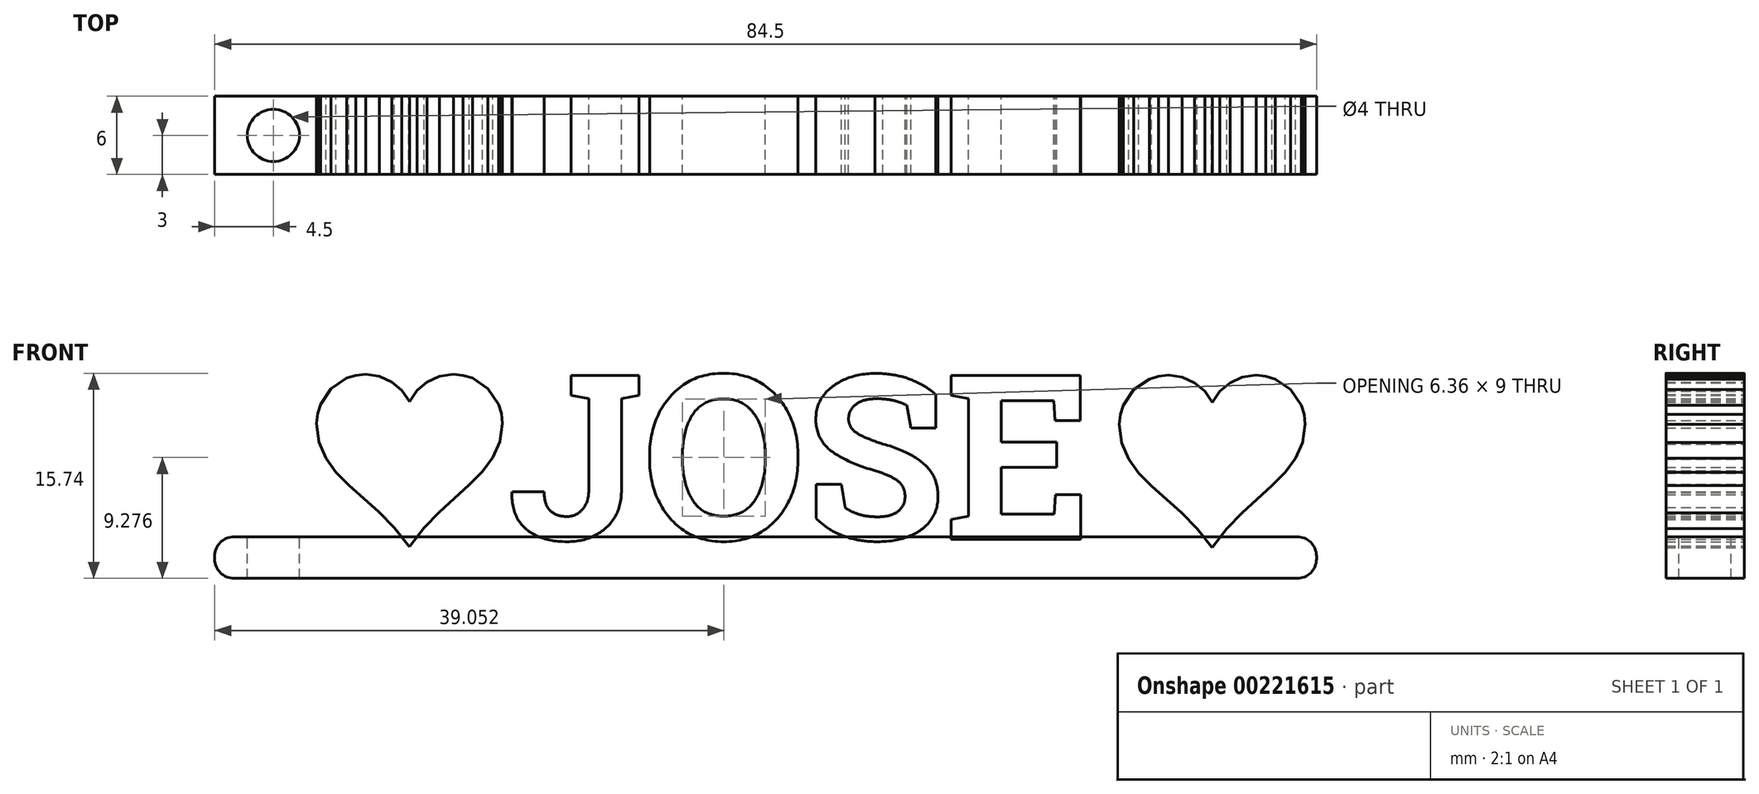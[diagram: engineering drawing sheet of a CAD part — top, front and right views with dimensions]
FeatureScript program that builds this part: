
annotation { "Feature Type Name" : "Feature", "Feature Type Description" : "" }
export const myFeature = defineFeature(function(context is Context, id is Id, definition is map)
    precondition{}
    {
        {
            var Q0;
            Q0=qCreatedBy(makeId("Front.planeOp"),FACE);
            var sketch = newSketch(context, id + "F0", { "sketchPlane" : qUnion([Q0])});
            skText(sketch, "E0", { "text": "   JOSE", "fontName": "RobotoSlab-Bold.ttf"});
            skLineSegment(sketch, "E1", {"start": v(45.25, 12.6) * mm, "end": v(44.49, 12.52) * mm});
            skLineSegment(sketch, "E2", {"start": v(44.49, 12.52) * mm, "end": v(43.78, 12.3) * mm});
            skLineSegment(sketch, "E3", {"start": v(43.78, 12.3) * mm, "end": v(42.58, 11.5) * mm});
            skLineSegment(sketch, "E4", {"start": v(42.58, 11.5) * mm, "end": v(41.78, 10.3) * mm});
            skLineSegment(sketch, "E5", {"start": v(41.78, 10.3) * mm, "end": v(41.56, 9.59) * mm});
            skLineSegment(sketch, "E6", {"start": v(41.56, 9.59) * mm, "end": v(41.48, 8.83) * mm});
            skLineSegment(sketch, "E7", {"start": v(41.48, 8.83) * mm, "end": v(41.67, 7.39) * mm});
            skLineSegment(sketch, "E8", {"start": v(41.67, 7.39) * mm, "end": v(42.19, 6.16) * mm});
            skLineSegment(sketch, "E9", {"start": v(42.19, 6.16) * mm, "end": v(42.98, 5.08) * mm});
            skLineSegment(sketch, "E10", {"start": v(42.98, 5.08) * mm, "end": v(43.96, 4.08) * mm});
            skLineSegment(sketch, "E11", {"start": v(43.96, 4.08) * mm, "end": v(46.26, 2.03) * mm});
            skLineSegment(sketch, "E12", {"start": v(46.26, 2.03) * mm, "end": v(47.44, 0.82) * mm});
            skLineSegment(sketch, "E13", {"start": v(47.44, 0.82) * mm, "end": v(48.56, -0.59) * mm});
            skLineSegment(sketch, "E14", {"start": v(48.56, -0.59) * mm, "end": v(48.6, -0.65) * mm});
            skLineSegment(sketch, "E15", {"start": v(48.6, -0.65) * mm, "end": v(48.65, -0.59) * mm});
            skLineSegment(sketch, "E16", {"start": v(48.65, -0.59) * mm, "end": v(49.73, 0.82) * mm});
            skLineSegment(sketch, "E17", {"start": v(49.73, 0.82) * mm, "end": v(50.9, 2.03) * mm});
            skLineSegment(sketch, "E18", {"start": v(50.9, 2.03) * mm, "end": v(53.2, 4.12) * mm});
            skLineSegment(sketch, "E19", {"start": v(53.2, 4.12) * mm, "end": v(54.2, 5.13) * mm});
            skLineSegment(sketch, "E20", {"start": v(54.2, 5.13) * mm, "end": v(55, 6.21) * mm});
            skLineSegment(sketch, "E21", {"start": v(55, 6.21) * mm, "end": v(55.54, 7.42) * mm});
            skLineSegment(sketch, "E22", {"start": v(55.54, 7.42) * mm, "end": v(55.73, 8.83) * mm});
            skLineSegment(sketch, "E23", {"start": v(55.73, 8.83) * mm, "end": v(55.66, 9.59) * mm});
            skLineSegment(sketch, "E24", {"start": v(55.66, 9.59) * mm, "end": v(55.44, 10.3) * mm});
            skLineSegment(sketch, "E25", {"start": v(55.44, 10.3) * mm, "end": v(54.63, 11.5) * mm});
            skLineSegment(sketch, "E26", {"start": v(54.63, 11.5) * mm, "end": v(53.43, 12.3) * mm});
            skLineSegment(sketch, "E27", {"start": v(53.43, 12.3) * mm, "end": v(52.72, 12.52) * mm});
            skLineSegment(sketch, "E28", {"start": v(52.72, 12.52) * mm, "end": v(51.97, 12.6) * mm});
            skLineSegment(sketch, "E29", {"start": v(51.97, 12.6) * mm, "end": v(50.9, 12.44) * mm});
            skLineSegment(sketch, "E30", {"start": v(50.9, 12.44) * mm, "end": v(49.96, 12.01) * mm});
            skLineSegment(sketch, "E31", {"start": v(49.96, 12.01) * mm, "end": v(49.18, 11.35) * mm});
            skLineSegment(sketch, "E32", {"start": v(49.18, 11.35) * mm, "end": v(48.6, 10.5) * mm});
            skLineSegment(sketch, "E33", {"start": v(48.6, 10.5) * mm, "end": v(48.03, 11.35) * mm});
            skLineSegment(sketch, "E34", {"start": v(48.03, 11.35) * mm, "end": v(47.25, 12.01) * mm});
            skLineSegment(sketch, "E35", {"start": v(47.25, 12.01) * mm, "end": v(46.3, 12.44) * mm});
            skLineSegment(sketch, "E36", {"start": v(46.3, 12.44) * mm, "end": v(45.25, 12.6) * mm});
            skLineSegment(sketch, "E37", {"start": v(39.6, 12.72) * mm, "end": v(70.68, 12.72) * mm, "construction": true});
            skLineSegment(sketch, "E38", {"start": v(-16.32, 12.66) * mm, "end": v(-17.08, 12.59) * mm});
            skLineSegment(sketch, "E39", {"start": v(-17.08, 12.59) * mm, "end": v(-17.78, 12.37) * mm});
            skLineSegment(sketch, "E40", {"start": v(-17.78, 12.37) * mm, "end": v(-18.98, 11.56) * mm});
            skLineSegment(sketch, "E41", {"start": v(-18.98, 11.56) * mm, "end": v(-19.79, 10.36) * mm});
            skLineSegment(sketch, "E42", {"start": v(-19.79, 10.36) * mm, "end": v(-20, 9.65) * mm});
            skLineSegment(sketch, "E43", {"start": v(-20, 9.65) * mm, "end": v(-20.09, 8.9) * mm});
            skLineSegment(sketch, "E44", {"start": v(-20.09, 8.9) * mm, "end": v(-19.9, 7.45) * mm});
            skLineSegment(sketch, "E45", {"start": v(-19.9, 7.45) * mm, "end": v(-19.38, 6.22) * mm});
            skLineSegment(sketch, "E46", {"start": v(-19.38, 6.22) * mm, "end": v(-18.6, 5.15) * mm});
            skLineSegment(sketch, "E47", {"start": v(-18.6, 5.15) * mm, "end": v(-17.6, 4.15) * mm});
            skLineSegment(sketch, "E48", {"start": v(-17.6, 4.15) * mm, "end": v(-15.31, 2.09) * mm});
            skLineSegment(sketch, "E49", {"start": v(-15.31, 2.09) * mm, "end": v(-14.13, 0.89) * mm});
            skLineSegment(sketch, "E50", {"start": v(-14.13, 0.89) * mm, "end": v(-13, -0.52) * mm});
            skLineSegment(sketch, "E51", {"start": v(-13, -0.52) * mm, "end": v(-12.96, -0.59) * mm});
            skLineSegment(sketch, "E52", {"start": v(-12.96, -0.59) * mm, "end": v(-12.92, -0.52) * mm});
            skLineSegment(sketch, "E53", {"start": v(-12.92, -0.52) * mm, "end": v(-11.84, 0.89) * mm});
            skLineSegment(sketch, "E54", {"start": v(-11.84, 0.89) * mm, "end": v(-10.67, 2.1) * mm});
            skLineSegment(sketch, "E55", {"start": v(-10.67, 2.1) * mm, "end": v(-8.37, 4.19) * mm});
            skLineSegment(sketch, "E56", {"start": v(-8.37, 4.19) * mm, "end": v(-7.37, 5.2) * mm});
            skLineSegment(sketch, "E57", {"start": v(-7.37, 5.2) * mm, "end": v(-6.56, 6.28) * mm});
            skLineSegment(sketch, "E58", {"start": v(-6.56, 6.28) * mm, "end": v(-6.03, 7.49) * mm});
            skLineSegment(sketch, "E59", {"start": v(-6.03, 7.49) * mm, "end": v(-5.83, 8.9) * mm});
            skLineSegment(sketch, "E60", {"start": v(-5.83, 8.9) * mm, "end": v(-5.91, 9.65) * mm});
            skLineSegment(sketch, "E61", {"start": v(-5.91, 9.65) * mm, "end": v(-6.13, 10.36) * mm});
            skLineSegment(sketch, "E62", {"start": v(-6.13, 10.36) * mm, "end": v(-6.94, 11.56) * mm});
            skLineSegment(sketch, "E63", {"start": v(-6.94, 11.56) * mm, "end": v(-8.13, 12.37) * mm});
            skLineSegment(sketch, "E64", {"start": v(-8.13, 12.37) * mm, "end": v(-8.84, 12.59) * mm});
            skLineSegment(sketch, "E65", {"start": v(-8.84, 12.59) * mm, "end": v(-9.6, 12.66) * mm});
            skLineSegment(sketch, "E66", {"start": v(-9.6, 12.66) * mm, "end": v(-10.66, 12.5) * mm});
            skLineSegment(sketch, "E67", {"start": v(-10.66, 12.5) * mm, "end": v(-11.6, 12.08) * mm});
            skLineSegment(sketch, "E68", {"start": v(-11.6, 12.08) * mm, "end": v(-12.38, 11.41) * mm});
            skLineSegment(sketch, "E69", {"start": v(-12.38, 11.41) * mm, "end": v(-12.96, 10.56) * mm});
            skLineSegment(sketch, "E70", {"start": v(-12.96, 10.56) * mm, "end": v(-13.54, 11.41) * mm});
            skLineSegment(sketch, "E71", {"start": v(-13.54, 11.41) * mm, "end": v(-14.32, 12.08) * mm});
            skLineSegment(sketch, "E72", {"start": v(-14.32, 12.08) * mm, "end": v(-15.26, 12.5) * mm});
            skLineSegment(sketch, "E73", {"start": v(-15.26, 12.5) * mm, "end": v(-16.32, 12.66) * mm});
            const initialGuessF0  = {"E0": [-0.0184, 0, 1, 0, 0.01272]};
            skSetInitialGuess(sketch, initialGuessF0);
            skSolve(sketch);
        }
        {
            var Q0;
            Q0=qSketchRegion(id+"F0",true);
            extrude(context, id + "F1", {"entities" : qUnion([Q0]), "endBound" : BoundingType.SYMMETRIC, "depth" : 6 * mm});
        }
        {
            var Q0;
            Q0=qCreatedBy(makeId("Top.planeOp"),FACE);
            var sketch = newSketch(context, id + "F2", { "sketchPlane" : qUnion([Q0])});
            skLineSegment(sketch, "E74.bottom", {"start": v(-20.4, 3) * mm, "end": v(56.6, 3) * mm});
            skLineSegment(sketch, "E74.top", {"start": v(-20.4, -3) * mm, "end": v(56.6, -3) * mm});
            skLineSegment(sketch, "E74.left", {"start": v(-20.4, 3) * mm, "end": v(-20.4, -3) * mm});
            skLineSegment(sketch, "E74.right", {"start": v(56.6, 3) * mm, "end": v(56.6, -3) * mm});
            skSolve(sketch);
        }
        {
            var Q0;
            Q0=makeQuery(id+"F2.imprint","IMPRINT",FACE,{"disambiguationData":[TD([[makeQuery(id+"F2.imprint","IMPRINT",EDGE,{"derivedFrom":sQuery(id+"F2.wireOp",EDGE,"E74.bottom")}),-1.0]])]});
            extrude(context, id + "F3", {"entities" : qUnion([Q0]), "depth" : 0.2 * mm});
        }
        {
            var Q0;
            Q0=makeQuery(id+"F3.opExtrude","CAP_FACE",FACE,{"disambiguationData":[OSD([sQuery(id+"F2.wireOp",EDGE,"E74.bottom"),sQuery(id+"F2.wireOp",EDGE,"E74.top"),sQuery(id+"F2.wireOp",EDGE,"E74.left"),sQuery(id+"F2.wireOp",EDGE,"E74.right")])],"isStart":true});
            extrude(context, id + "F4", {"entities" : qUnion([Q0]), "depth" : 3 * mm});
        }
        {
            var Q0;
            {var subQ0=sQuery(id+"F2.wireOp",EDGE,"E74.left");Q0=makeQuery(id+"FaVoHrOpcFZXiYX_6.opBoolean","MERGE",FACE,{"derivedFrom":[makeQuery(id+"F3.opExtrude","SWEPT_FACE",FACE,{"disambiguationData":[OSD([subQ0])]}),makeQuery(id+"F4.opExtrude","SWEPT_FACE",FACE,{"disambiguationData":[OSD([subQ0])]})]});}
            var sketch = newSketch(context, id + "F5", { "sketchPlane" : qUnion([Q0])});
            skLineSegment(sketch, "E75.bottom", {"start": v(-3, -3) * mm, "end": v(3, -3) * mm});
            skLineSegment(sketch, "E75.top", {"start": v(-3, 0.2) * mm, "end": v(3, 0.2) * mm});
            skLineSegment(sketch, "E75.left", {"start": v(-3, -3) * mm, "end": v(-3, 0.2) * mm});
            skLineSegment(sketch, "E75.right", {"start": v(3, -3) * mm, "end": v(3, 0.2) * mm});
            skSolve(sketch);
        }
        {
            var Q0;
            Q0=qSketchRegion(id+"F5",true);
            extrude(context, id + "F6", {"entities" : qUnion([Q0]), "operationType" : NewBodyOperationType.ADD, "depth" : 7.5 * mm});
        }
        {
            var Q0;
            Q0=makeQuery(id+"F6.opExtrude","CAP_EDGE",EDGE,{"disambiguationData":[OSD([sQuery(id+"F5.wireOp",EDGE,"E75.bottom")])],"isStart":false});
            var Q1;
            Q1=makeQuery(id+"F6.opExtrude","CAP_EDGE",EDGE,{"disambiguationData":[OSD([sQuery(id+"F5.wireOp",EDGE,"E75.top")])],"isStart":false});
            var Q2;
            Q2=makeQuery(id+"F4.opExtrude","CAP_EDGE",EDGE,{"disambiguationData":[OSD([sQuery(id+"F2.wireOp",EDGE,"E74.right")])],"isStart":false});
            fillet(context, id + "F7", {"entities" : qUnion([Q0, Q1, Q2]), "radius" : 1.5 * mm, "tangentPropagation" : true, "allowEdgeOverflow" : false});
        }
        {
            var Q0;
            {var subQ19=sQuery(id+"F2.wireOp",EDGE,"E74.top");var subQ20=sQuery(id+"F2.wireOp",EDGE,"E74.bottom");var subQ63=sQuery(id+"F0.wireOp",EDGE,"E0.sketch_text.stroke-2");var subQ66=sQuery(id+"F2.wireOp",EDGE,"E74.left");Q0=makeQuery(id+"F6.boolean.opBoolean","MERGE",FACE,{"derivedFrom":[makeQuery(id+"FaVoHrOpcFZXiYX_6.opBoolean","SPLIT",FACE,{"disambiguationData":[TD([makeQuery(id+"F1.opExtrude","SWEPT_FACE",FACE,{"disambiguationData":[OSD([subQ63])]})])],"derivedFrom":makeQuery(id+"F3.opExtrude","CAP_FACE",FACE,{"disambiguationData":[OSD([subQ20,subQ19,subQ66,sQuery(id+"F2.wireOp",EDGE,"E74.right")])],"isStart":false})}),makeQuery(id+"F6.opExtrude","SWEPT_FACE",FACE,{"disambiguationData":[OSD([sQuery(id+"F5.wireOp",EDGE,"E75.top")])]})]});}
            var sketch = newSketch(context, id + "F8", { "sketchPlane" : qUnion([Q0])});
            skCircle(sketch, "E76", {"center": v(-23.4, 0) * mm, "radius": 2 * mm});
            skSolve(sketch);
        }
        {
            var Q0;
            Q0=makeQuery(id+"F8.imprint","IMPRINT",FACE,{"disambiguationData":[TD([[makeQuery(id+"F8.imprint","IMPRINT",EDGE,{"derivedFrom":sQuery(id+"F8.wireOp",EDGE,"E76")}),1.0]])]});
            extrude(context, id + "F9", {"entities" : qUnion([Q0]), "operationType" : NewBodyOperationType.REMOVE, "oppositeDirection" : true, "depth" : 4 * mm});
        }
        {
            var Q0;
            Q0=makeQuery(id+"F3.opExtrude","CAP_EDGE",EDGE,{"disambiguationData":[OSD([sQuery(id+"F2.wireOp",EDGE,"E74.right")])],"isStart":false});
            fillet(context, id + "F10", {"entities" : qUnion([Q0]), "radius" : 1.5 * mm, "tangentPropagation" : true, "allowEdgeOverflow" : false});
        }
    });
